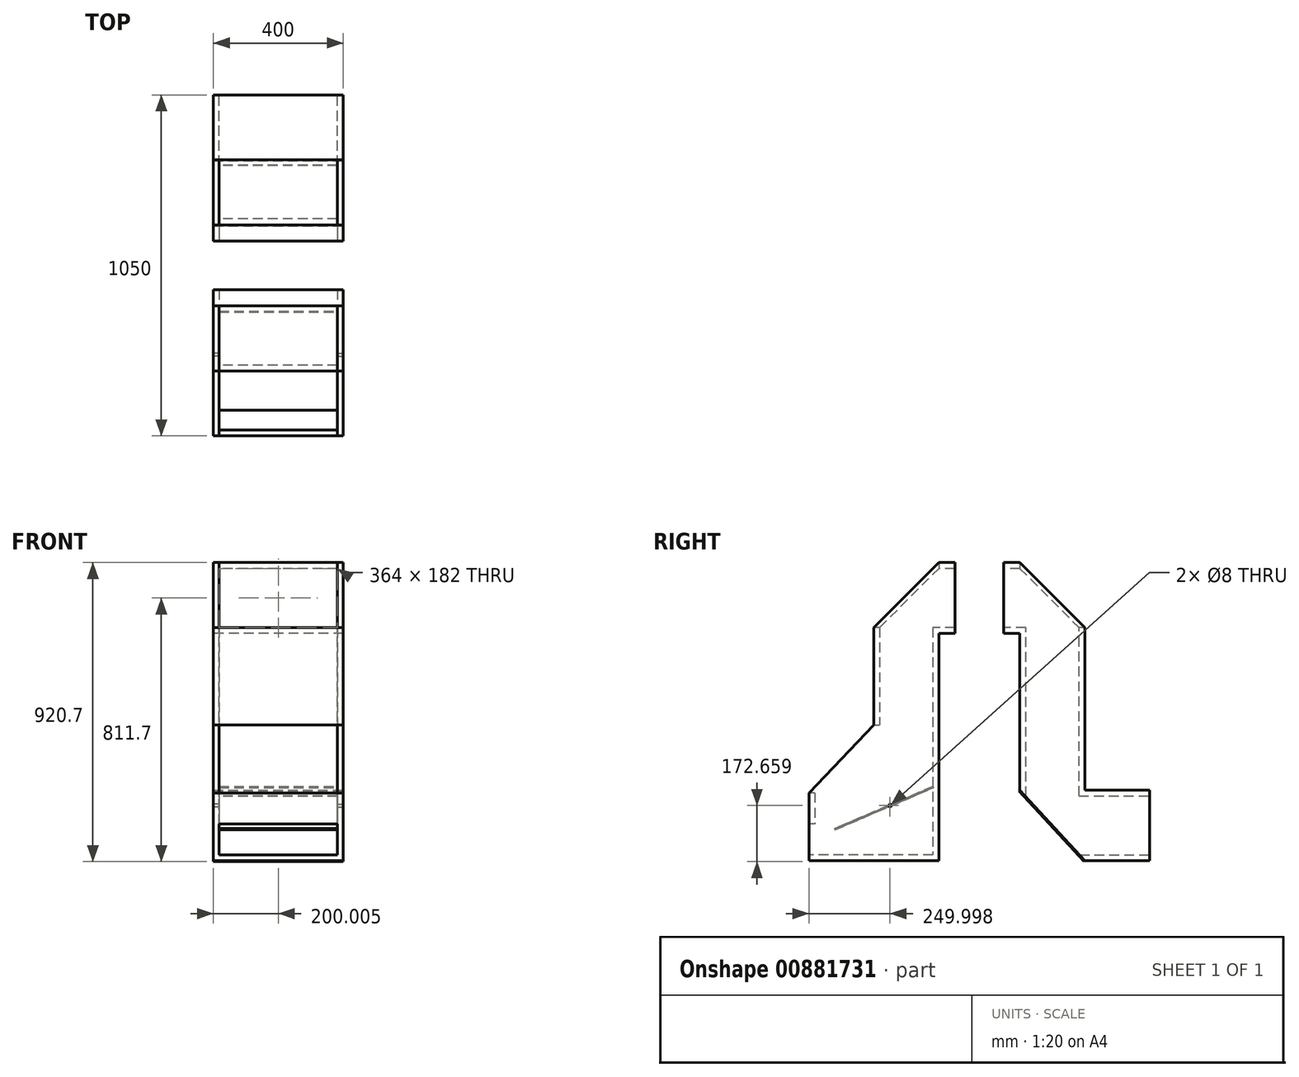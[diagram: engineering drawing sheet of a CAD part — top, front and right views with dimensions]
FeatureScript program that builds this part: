
annotation { "Feature Type Name" : "Feature", "Feature Type Description" : "" }
export const myFeature = defineFeature(function(context is Context, id is Id, definition is map)
    precondition{}
    {
        {
            var Q0;
            Q0=qCreatedBy(makeId("Top.planeOp"),FACE);
            var sketch = newSketch(context, id + "F0", { "sketchPlane" : qUnion([Q0])});
            skLineSegment(sketch, "E0.bottom", {"start": v(-193.3, 234.15) * mm, "end": v(206.7, 234.15) * mm});
            skLineSegment(sketch, "E0.top", {"start": v(-193.3, -165.85) * mm, "end": v(206.7, -165.85) * mm});
            skLineSegment(sketch, "E0.left", {"start": v(-193.3, 234.15) * mm, "end": v(-193.3, -165.85) * mm});
            skLineSegment(sketch, "E0.right", {"start": v(206.7, 234.15) * mm, "end": v(206.7, -165.85) * mm});
            skSolve(sketch);
        }
        {
            var Q0;
            Q0 = qSketchRegion(id + "F0", true);
            extrude(context, id + "F1", {"entities" : qUnion([Q0]), "oppositeDirection" : true, "depth" : 18 * mm, "offsetDistance" : 25 * mm});
        }
        {
            var Q0;
            Q0=makeQuery(id+"F1.opExtrude","CAP_FACE",FACE,{"disambiguationData":[OSD([sQuery(id+"F0.wireOp",EDGE,"E0.bottom"),sQuery(id+"F0.wireOp",EDGE,"E0.top"),sQuery(id+"F0.wireOp",EDGE,"E0.left"),sQuery(id+"F0.wireOp",EDGE,"E0.right")])],"isStart":true});
            var sketch = newSketch(context, id + "F2", { "sketchPlane" : qUnion([Q0])});
            skLineSegment(sketch, "E1.bottom", {"start": v(206.7, 234.15) * mm, "end": v(188.7, 234.15) * mm});
            skLineSegment(sketch, "E1.top", {"start": v(206.7, -165.85) * mm, "end": v(188.7, -165.85) * mm});
            skLineSegment(sketch, "E1.left", {"start": v(206.7, 234.15) * mm, "end": v(206.7, -165.85) * mm});
            skLineSegment(sketch, "E1.right", {"start": v(188.7, 234.15) * mm, "end": v(188.7, -165.85) * mm});
            skLineSegment(sketch, "E2.bottom", {"start": v(-193.3, 234.15) * mm, "end": v(-175.3, 234.15) * mm});
            skLineSegment(sketch, "E2.top", {"start": v(-193.3, -165.85) * mm, "end": v(-175.3, -165.85) * mm});
            skLineSegment(sketch, "E2.left", {"start": v(-193.3, 234.15) * mm, "end": v(-193.3, -165.85) * mm});
            skLineSegment(sketch, "E2.right", {"start": v(-175.3, 234.15) * mm, "end": v(-175.3, -165.85) * mm});
            skLineSegment(sketch, "E3.bottom", {"start": v(-175.3, 234.15) * mm, "end": v(188.7, 234.15) * mm});
            skLineSegment(sketch, "E3.top", {"start": v(-175.3, 216.15) * mm, "end": v(188.7, 216.15) * mm});
            skLineSegment(sketch, "E3.left", {"start": v(-175.3, 234.15) * mm, "end": v(-175.3, 216.15) * mm});
            skLineSegment(sketch, "E3.right", {"start": v(188.7, 234.15) * mm, "end": v(188.7, 216.15) * mm});
            skLineSegment(sketch, "E4.bottom", {"start": v(-175.3, -165.85) * mm, "end": v(188.7, -165.85) * mm});
            skLineSegment(sketch, "E4.top", {"start": v(-175.3, -147.85) * mm, "end": v(188.7, -147.85) * mm});
            skLineSegment(sketch, "E4.left", {"start": v(-175.3, -165.85) * mm, "end": v(-175.3, -147.85) * mm});
            skLineSegment(sketch, "E4.right", {"start": v(188.7, -165.85) * mm, "end": v(188.7, -147.85) * mm});
            skSolve(sketch);
        }
        {
            var Q0;
            Q0=makeQuery(id+"F2.imprint","IMPRINT",FACE,{"disambiguationData":[TD([[makeQuery(id+"F2.imprint","IMPRINT",EDGE,{"derivedFrom":sQuery(id+"F2.wireOp",EDGE,"E2.bottom")}),-1.0]])]});
            var Q1;
            Q1=makeQuery(id+"F2.imprint","IMPRINT",FACE,{"disambiguationData":[TD([[makeQuery(id+"F2.imprint","IMPRINT",EDGE,{"derivedFrom":sQuery(id+"F2.wireOp",EDGE,"E1.bottom")}),-1.0]])]});
            extrude(context, id + "F3", {"entities" : qUnion([Q0, Q1]), "operationType" : NewBodyOperationType.ADD, "depth" : 400 * mm, "offsetDistance" : 25 * mm});
        }
        {
            var Q0;
            Q0=makeQuery(id+"F2.imprint","IMPRINT",FACE,{"disambiguationData":[TD([[makeQuery(id+"F2.imprint","IMPRINT",EDGE,{"derivedFrom":sQuery(id+"F2.wireOp",EDGE,"E3.bottom")}),-1.0]])]});
            extrude(context, id + "F4", {"entities" : qUnion([Q0]), "operationType" : NewBodyOperationType.ADD, "depth" : 700 * mm, "offsetDistance" : 25 * mm});
        }
        {
            var Q0;
            Q0=makeQuery(id+"F3.boolean.opBoolean","MERGE",FACE,{"derivedFrom":[makeQuery(id+"F1.opExtrude","SWEPT_FACE",FACE,{"disambiguationData":[OSD([sQuery(id+"F0.wireOp",EDGE,"E0.right")])]}),makeQuery(id+"F3.opExtrude","SWEPT_FACE",FACE,{"disambiguationData":[OSD([sQuery(id+"F2.wireOp",EDGE,"E1.left")])]})]});
            var sketch = newSketch(context, id + "F5", { "sketchPlane" : qUnion([Q0])});
            skLineSegment(sketch, "E5", {"start": v(-165.85, 191) * mm, "end": v(34.15, 400) * mm});
            skSolve(sketch);
        }
        {
            var Q0;
            Q0=makeQuery(id+"F2.imprint","IMPRINT",FACE,{"disambiguationData":[TD([[makeQuery(id+"F2.imprint","IMPRINT",EDGE,{"derivedFrom":sQuery(id+"F2.wireOp",EDGE,"E4.bottom")}),1.0]])]});
            extrude(context, id + "F6", {"entities" : qUnion([Q0]), "operationType" : NewBodyOperationType.ADD, "depth" : (200 - 9) * mm, "offsetDistance" : 25 * mm});
        }
        {
            var Q0;
            Q0=makeQuery(id+"F6.boolean.opBoolean","MERGE",FACE,{"derivedFrom":[makeQuery(id+"F3.boolean.opBoolean","MERGE",FACE,{"derivedFrom":[makeQuery(id+"F1.opExtrude","SWEPT_FACE",FACE,{"disambiguationData":[OSD([sQuery(id+"F0.wireOp",EDGE,"E0.top")])]}),makeQuery(id+"F3.opExtrude","SWEPT_FACE",FACE,{"disambiguationData":[OSD([sQuery(id+"F2.wireOp",EDGE,"E1.top")])]}),makeQuery(id+"F3.opExtrude","SWEPT_FACE",FACE,{"disambiguationData":[OSD([sQuery(id+"F2.wireOp",EDGE,"E2.top")])]})]}),makeQuery(id+"F6.opExtrude","SWEPT_FACE",FACE,{"disambiguationData":[OSD([sQuery(id+"F2.wireOp",EDGE,"E4.bottom")])]})]});
            var sketch = newSketch(context, id + "F7", { "sketchPlane" : qUnion([Q0])});
            skLineSegment(sketch, "E6.bottom", {"start": v(-175.3, 0) * mm, "end": v(188.7, 0) * mm});
            skLineSegment(sketch, "E6.top", {"start": v(-175.3, 95.5) * mm, "end": v(188.7, 95.5) * mm});
            skLineSegment(sketch, "E6.left", {"start": v(-175.3, 0) * mm, "end": v(-175.3, 95.5) * mm});
            skLineSegment(sketch, "E6.right", {"start": v(188.7, 0) * mm, "end": v(188.7, 95.5) * mm});
            skSolve(sketch);
        }
        {
            var Q0;
            Q0 = qSketchRegion(id + "F7", true);
            extrude(context, id + "F8", {"entities" : qUnion([Q0]), "operationType" : NewBodyOperationType.REMOVE, "oppositeDirection" : true, "depth" : 25 * mm, "offsetDistance" : 25 * mm});
        }
        {
            var Q0;
            {var subQ0=sQuery(id+"F5.wireOp",EDGE,"E5");Q0=makeQuery(id+"F5.imprint","IMPRINT",FACE,{"disambiguationData":[TD([[makeQuery(id+"F5.imprint","IMPRINT",EDGE,{"derivedFrom":subQ0}),1.0]])]});}
            extrude(context, id + "F9", {"entities" : qUnion([Q0]), "operationType" : NewBodyOperationType.REMOVE, "endBound" : BoundingType.THROUGH_ALL, "oppositeDirection" : true, "depth" : 25 * mm, "offsetDistance" : 25 * mm});
        }
        {
            var Q0;
            Q0=makeQuery(id+"F3.opExtrude","CAP_FACE",FACE,{"disambiguationData":[OSD([sQuery(id+"F2.wireOp",EDGE,"E2.bottom"),sQuery(id+"F2.wireOp",EDGE,"E2.top"),sQuery(id+"F2.wireOp",EDGE,"E2.left"),sQuery(id+"F2.wireOp",EDGE,"E2.right"),sQuery(id+"F2.wireOp",EDGE,"E3.left"),sQuery(id+"F2.wireOp",EDGE,"E4.left")])],"isStart":false});
            extrude(context, id + "F10", {"entities" : qUnion([Q0]), "operationType" : NewBodyOperationType.ADD, "depth" : 300 * mm, "offsetDistance" : 25 * mm});
        }
        {
            var Q0;
            Q0=makeQuery(id+"F3.opExtrude","CAP_FACE",FACE,{"disambiguationData":[OSD([sQuery(id+"F2.wireOp",EDGE,"E1.bottom"),sQuery(id+"F2.wireOp",EDGE,"E1.top"),sQuery(id+"F2.wireOp",EDGE,"E1.left"),sQuery(id+"F2.wireOp",EDGE,"E1.right"),sQuery(id+"F2.wireOp",EDGE,"E3.right"),sQuery(id+"F2.wireOp",EDGE,"E4.right")])],"isStart":false});
            extrude(context, id + "F11", {"entities" : qUnion([Q0]), "operationType" : NewBodyOperationType.ADD, "depth" : 300 * mm, "offsetDistance" : 25 * mm});
        }
        {
            var Q0;
            {var subQ0=sQuery(id+"F2.wireOp",EDGE,"E4.left");var subQ1=sQuery(id+"F2.wireOp",EDGE,"E3.left");var subQ2=sQuery(id+"F2.wireOp",EDGE,"E2.right");Q0=makeQuery(id+"F10.boolean.opBoolean","MERGE",FACE,{"derivedFrom":[makeQuery(id+"F8.boolean.opBoolean","MERGE",FACE,{"derivedFrom":[makeQuery(id+"F3.opExtrude","SWEPT_FACE",FACE,{"disambiguationData":[OSD([subQ2,subQ1,subQ0])]})],"fromTools":[makeQuery(id+"F8.opExtrude","SWEPT_FACE",FACE,{"disambiguationData":[OSD([sQuery(id+"F7.wireOp",EDGE,"E6.left")])]})]}),makeQuery(id+"F10.opExtrude","SWEPT_FACE",FACE,{"disambiguationData":[OSD([subQ2,subQ1,subQ0])]})]});}
            var sketch = newSketch(context, id + "F12", { "sketchPlane" : qUnion([Q0])});
            skLineSegment(sketch, "E7.bottom", {"start": v(34.15, 700) * mm, "end": v(52.15, 700) * mm});
            skLineSegment(sketch, "E7.top", {"start": v(34.15, 400) * mm, "end": v(52.15, 400) * mm});
            skLineSegment(sketch, "E7.left", {"start": v(34.15, 700) * mm, "end": v(34.15, 400) * mm});
            skLineSegment(sketch, "E7.right", {"start": v(52.15, 700) * mm, "end": v(52.15, 400) * mm});
            skSolve(sketch);
        }
        {
            var Q0;
            Q0=makeQuery(id+"F12.imprint","IMPRINT",FACE,{"disambiguationData":[TD([[makeQuery(id+"F12.imprint","IMPRINT",EDGE,{"derivedFrom":sQuery(id+"F12.wireOp",EDGE,"E7.bottom")}),1.0]])]});
            var Q1;
            {var subQ0=sQuery(id+"F2.wireOp",EDGE,"E4.right");var subQ1=sQuery(id+"F2.wireOp",EDGE,"E3.right");var subQ2=sQuery(id+"F2.wireOp",EDGE,"E1.right");Q1=makeQuery(id+"F11.boolean.opBoolean","MERGE",FACE,{"derivedFrom":[makeQuery(id+"F8.boolean.opBoolean","MERGE",FACE,{"derivedFrom":[makeQuery(id+"F3.opExtrude","SWEPT_FACE",FACE,{"disambiguationData":[OSD([subQ2,subQ1,subQ0])]})],"fromTools":[makeQuery(id+"F8.opExtrude","SWEPT_FACE",FACE,{"disambiguationData":[OSD([sQuery(id+"F7.wireOp",EDGE,"E6.right")])]})]}),makeQuery(id+"F11.opExtrude","SWEPT_FACE",FACE,{"disambiguationData":[OSD([subQ2,subQ1,subQ0])]})]});}
            extrude(context, id + "F13", {"entities" : qUnion([Q0]), "operationType" : NewBodyOperationType.ADD, "endBound" : BoundingType.UP_TO_SURFACE, "depth" : 25 * mm, "endBoundEntityFace" : qUnion([Q1]), "offsetDistance" : 25 * mm});
        }
        {
            var Q0;
            {var subQ0=sQuery(id+"F2.wireOp",EDGE,"E1.left");Q0=makeQuery(id+"F11.boolean.opBoolean","MERGE",FACE,{"derivedFrom":[makeQuery(id+"F3.boolean.opBoolean","MERGE",FACE,{"derivedFrom":[makeQuery(id+"F1.opExtrude","SWEPT_FACE",FACE,{"disambiguationData":[OSD([sQuery(id+"F0.wireOp",EDGE,"E0.right")])]}),makeQuery(id+"F3.opExtrude","SWEPT_FACE",FACE,{"disambiguationData":[OSD([subQ0])]})]}),makeQuery(id+"F11.opExtrude","SWEPT_FACE",FACE,{"disambiguationData":[OSD([subQ0])]})]});}
            var sketch = newSketch(context, id + "F14", { "sketchPlane" : qUnion([Q0])});
            skLineSegment(sketch, "E8", {"start": v(-65.85, 295.5) * mm, "end": v(234.15, 8.42) * mm});
            skPoint(sketch, "E9", {"position": v(84.15, 151.96) * mm});
            skCircle(sketch, "E10", {"center": v(84.15, 151.96) * mm, "radius": 150 * mm});
            skCircle(sketch, "E11", {"center": v(84.15, 151.96) * mm, "radius": 4 * mm});
            skLineSegment(sketch, "E12", {"start": v(84.15, 151.96) * mm, "end": v(234.15, 151.96) * mm});
            skLineSegment(sketch, "E13", {"start": v(84.15, 151.96) * mm, "end": v(84.15, 301.96) * mm});
            skLineSegment(sketch, "E14", {"start": v(84.15, 151.96) * mm, "end": v(187.86, 260.33) * mm});
            skPoint(sketch, "E15", {"position": v(211, 206.15) * mm});
            skLineSegment(sketch, "E16", {"start": v(84.15, 151.96) * mm, "end": v(222.1, 210.88) * mm});
            skLineSegment(sketch, "E17", {"start": v(84.15, 151.96) * mm, "end": v(-53.8, 93.04) * mm});
            skSolve(sketch);
        }
        {
            var Q0;
            {var subQ0=sQuery(id+"F2.wireOp",EDGE,"E4.right");var subQ1=sQuery(id+"F2.wireOp",EDGE,"E3.right");var subQ2=sQuery(id+"F2.wireOp",EDGE,"E1.right");Q0=makeQuery(id+"F11.boolean.opBoolean","MERGE",FACE,{"derivedFrom":[makeQuery(id+"F8.boolean.opBoolean","MERGE",FACE,{"derivedFrom":[makeQuery(id+"F3.opExtrude","SWEPT_FACE",FACE,{"disambiguationData":[OSD([subQ2,subQ1,subQ0])]})],"fromTools":[makeQuery(id+"F8.opExtrude","SWEPT_FACE",FACE,{"disambiguationData":[OSD([sQuery(id+"F7.wireOp",EDGE,"E6.right")])]})]}),makeQuery(id+"F11.opExtrude","SWEPT_FACE",FACE,{"disambiguationData":[OSD([subQ2,subQ1,subQ0])]})]});}
            var sketch = newSketch(context, id + "F15", { "sketchPlane" : qUnion([Q0])});
            skLineSegment(sketch, "E18", {"start": v(-216.42, 210.63) * mm, "end": v(87.06, 81) * mm});
            skLineSegment(sketch, "E19", {"start": v(85.48, 77.32) * mm, "end": v(-217.99, 206.96) * mm});
            skPoint(sketch, "E20", {"position": v(-84.15, 151.96) * mm});
            skLineSegment(sketch, "E21", {"start": v(85.48, 77.32) * mm, "end": v(87.06, 81) * mm});
            skLineSegment(sketch, "E22", {"start": v(-216.42, 210.63) * mm, "end": v(-217.99, 206.96) * mm});
            skSolve(sketch);
        }
        {
            var Q0;
            Q0 = qSketchRegion(id + "F15", true);
            var Q1;
            {var subQ0=sQuery(id+"F2.wireOp",EDGE,"E4.left");var subQ1=sQuery(id+"F2.wireOp",EDGE,"E3.left");var subQ2=sQuery(id+"F2.wireOp",EDGE,"E2.right");Q1=makeQuery(id+"F10.boolean.opBoolean","MERGE",FACE,{"derivedFrom":[makeQuery(id+"F8.boolean.opBoolean","MERGE",FACE,{"derivedFrom":[makeQuery(id+"F3.opExtrude","SWEPT_FACE",FACE,{"disambiguationData":[OSD([subQ2,subQ1,subQ0])]})],"fromTools":[makeQuery(id+"F8.opExtrude","SWEPT_FACE",FACE,{"disambiguationData":[OSD([sQuery(id+"F7.wireOp",EDGE,"E6.left")])]})]}),makeQuery(id+"F10.opExtrude","SWEPT_FACE",FACE,{"disambiguationData":[OSD([subQ2,subQ1,subQ0])]})]});}
            extrude(context, id + "F16", {"entities" : qUnion([Q0]), "endBound" : BoundingType.UP_TO_SURFACE, "depth" : 25 * mm, "endBoundEntityFace" : qUnion([Q1]), "offsetDistance" : 25 * mm});
        }
        {
            var Q0;
            {var subQ1=sQuery(id+"F14.wireOp",EDGE,"E8");var subQ3=sQuery(id+"F14.wireOp",EDGE,"E11");var subQ4=makeQuery(id+"F14.imprint","INTERSECT",VERTEX,{"disambiguationData":[OD(1.0)],"derivedFrom":[subQ1,subQ3]});Q0=makeQuery(id+"F14.imprint","IMPRINT",FACE,{"disambiguationData":[TD([[makeQuery(id+"F14.imprint","IMPRINT",EDGE,{"disambiguationData":[TD([[subQ4,1.0]])],"derivedFrom":subQ3}),1.0]])]});}
            var Q1;
            {var subQ1=sQuery(id+"F14.wireOp",EDGE,"E8");var subQ3=sQuery(id+"F14.wireOp",EDGE,"E11");var subQ4=makeQuery(id+"F14.imprint","INTERSECT",VERTEX,{"disambiguationData":[OD(0.0)],"derivedFrom":[subQ1,subQ3]});Q1=makeQuery(id+"F14.imprint","IMPRINT",FACE,{"disambiguationData":[TD([[makeQuery(id+"F14.imprint","IMPRINT",EDGE,{"disambiguationData":[TD([[subQ4,-1.0]])],"derivedFrom":subQ3}),1.0]])]});}
            var Q2;
            {var subQ1=sQuery(id+"F14.wireOp",EDGE,"E8");var subQ3=sQuery(id+"F14.wireOp",EDGE,"E11");var subQ4=makeQuery(id+"F14.imprint","INTERSECT",VERTEX,{"disambiguationData":[OD(0.0)],"derivedFrom":[subQ1,subQ3]});Q2=makeQuery(id+"F14.imprint","IMPRINT",FACE,{"disambiguationData":[TD([[makeQuery(id+"F14.imprint","IMPRINT",EDGE,{"disambiguationData":[TD([[subQ4,1.0]])],"derivedFrom":subQ3}),1.0]])]});}
            var Q3;
            {var subQ0=sQuery(id+"F14.wireOp",EDGE,"E14");var subQ1=sQuery(id+"F14.wireOp",EDGE,"E11");var subQ2=makeQuery(id+"F14.imprint","INTERSECT",VERTEX,{"derivedFrom":[subQ1,subQ0]});Q3=makeQuery(id+"F14.imprint","IMPRINT",FACE,{"disambiguationData":[TD([[makeQuery(id+"F14.imprint","IMPRINT",EDGE,{"disambiguationData":[TD([[subQ2,-1.0]])],"derivedFrom":subQ1}),1.0]])]});}
            var Q4;
            {var subQ0=sQuery(id+"F14.wireOp",EDGE,"E16");var subQ1=sQuery(id+"F14.wireOp",EDGE,"E11");var subQ2=makeQuery(id+"F14.imprint","INTERSECT",VERTEX,{"derivedFrom":[subQ1,subQ0]});Q4=makeQuery(id+"F14.imprint","IMPRINT",FACE,{"disambiguationData":[TD([[makeQuery(id+"F14.imprint","IMPRINT",EDGE,{"disambiguationData":[TD([[subQ2,-1.0]])],"derivedFrom":subQ1}),1.0]])]});}
            var Q5;
            {var subQ0=sQuery(id+"F14.wireOp",EDGE,"E16");var subQ1=sQuery(id+"F14.wireOp",EDGE,"E11");var subQ2=makeQuery(id+"F14.imprint","INTERSECT",VERTEX,{"derivedFrom":[subQ1,subQ0]});Q5=makeQuery(id+"F14.imprint","IMPRINT",FACE,{"disambiguationData":[TD([[makeQuery(id+"F14.imprint","IMPRINT",EDGE,{"disambiguationData":[TD([[subQ2,1.0]])],"derivedFrom":subQ1}),1.0]])]});}
            var Q6;
            {var subQ1=sQuery(id+"F14.wireOp",EDGE,"E8");var subQ3=sQuery(id+"F14.wireOp",EDGE,"E11");var subQ4=makeQuery(id+"F14.imprint","INTERSECT",VERTEX,{"disambiguationData":[OD(1.0)],"derivedFrom":[subQ1,subQ3]});Q6=makeQuery(id+"F14.imprint","IMPRINT",FACE,{"disambiguationData":[TD([[makeQuery(id+"F14.imprint","IMPRINT",EDGE,{"disambiguationData":[TD([[subQ4,-1.0]])],"derivedFrom":subQ3}),1.0]])]});}
            extrude(context, id + "F17", {"entities" : qUnion([Q0, Q1, Q2, Q3, Q4, Q5, Q6]), "operationType" : NewBodyOperationType.REMOVE, "oppositeDirection" : true, "depth" : 18 * mm, "offsetDistance" : 25 * mm});
        }
        {
            var Q0;
            {var subQ0=sQuery(id+"F2.wireOp",EDGE,"E2.left");Q0=makeQuery(id+"F10.boolean.opBoolean","MERGE",FACE,{"derivedFrom":[makeQuery(id+"F3.boolean.opBoolean","MERGE",FACE,{"derivedFrom":[makeQuery(id+"F1.opExtrude","SWEPT_FACE",FACE,{"disambiguationData":[OSD([sQuery(id+"F0.wireOp",EDGE,"E0.left")])]}),makeQuery(id+"F3.opExtrude","SWEPT_FACE",FACE,{"disambiguationData":[OSD([subQ0])]})]}),makeQuery(id+"F10.opExtrude","SWEPT_FACE",FACE,{"disambiguationData":[OSD([subQ0])]})]});}
            var sketch = newSketch(context, id + "F18", { "sketchPlane" : qUnion([Q0])});
            skPoint(sketch, "E23", {"position": v(-84.15, 151.96) * mm});
            skCircle(sketch, "E24", {"center": v(-84.15, 151.96) * mm, "radius": 4 * mm});
            skSolve(sketch);
        }
        {
            var Q0;
            Q0 = qSketchRegion(id + "F18", true);
            extrude(context, id + "F19", {"entities" : qUnion([Q0]), "operationType" : NewBodyOperationType.REMOVE, "oppositeDirection" : true, "depth" : 18 * mm, "offsetDistance" : 25 * mm});
        }
        {
            var Q0;
            {var subQ0=sQuery(id+"F2.wireOp",EDGE,"E3.right");var subQ1=sQuery(id+"F2.wireOp",EDGE,"E3.left");Q0=makeQuery(id+"F13.boolean.opBoolean","MERGE",FACE,{"derivedFrom":[makeQuery(id+"F11.boolean.opBoolean","MERGE",FACE,{"derivedFrom":[makeQuery(id+"F10.boolean.opBoolean","MERGE",FACE,{"derivedFrom":[makeQuery(id+"F4.opExtrude","CAP_FACE",FACE,{"disambiguationData":[OSD([sQuery(id+"F2.wireOp",EDGE,"E3.bottom"),sQuery(id+"F2.wireOp",EDGE,"E3.top"),subQ1,subQ0])],"isStart":false}),makeQuery(id+"F10.opExtrude","CAP_FACE",FACE,{"disambiguationData":[OSD([sQuery(id+"F2.wireOp",EDGE,"E2.bottom"),sQuery(id+"F2.wireOp",EDGE,"E2.top"),sQuery(id+"F2.wireOp",EDGE,"E2.left"),sQuery(id+"F2.wireOp",EDGE,"E2.right"),subQ1,sQuery(id+"F2.wireOp",EDGE,"E4.left")])],"isStart":false})]}),makeQuery(id+"F11.opExtrude","CAP_FACE",FACE,{"disambiguationData":[OSD([sQuery(id+"F2.wireOp",EDGE,"E1.bottom"),sQuery(id+"F2.wireOp",EDGE,"E1.top"),sQuery(id+"F2.wireOp",EDGE,"E1.left"),sQuery(id+"F2.wireOp",EDGE,"E1.right"),subQ0,sQuery(id+"F2.wireOp",EDGE,"E4.right")])],"isStart":false})]}),makeQuery(id+"F13.opExtrude","SWEPT_FACE",FACE,{"disambiguationData":[OSD([sQuery(id+"F12.wireOp",EDGE,"E7.bottom")])]})]});}
            var sketch = newSketch(context, id + "F20", { "sketchPlane" : qUnion([Q0])});
            skLineSegment(sketch, "E25.bottom", {"start": v(-193.3, 234.15) * mm, "end": v(-175.3, 234.15) * mm});
            skLineSegment(sketch, "E25.top", {"start": v(-193.3, 34.15) * mm, "end": v(-175.3, 34.15) * mm});
            skLineSegment(sketch, "E25.left", {"start": v(-193.3, 234.15) * mm, "end": v(-193.3, 34.15) * mm});
            skLineSegment(sketch, "E25.right", {"start": v(-175.3, 234.15) * mm, "end": v(-175.3, 34.15) * mm});
            skLineSegment(sketch, "E26.bottom", {"start": v(206.7, 234.15) * mm, "end": v(188.7, 234.15) * mm});
            skLineSegment(sketch, "E26.top", {"start": v(206.7, 34.15) * mm, "end": v(188.7, 34.15) * mm});
            skLineSegment(sketch, "E26.left", {"start": v(206.7, 234.15) * mm, "end": v(206.7, 34.15) * mm});
            skLineSegment(sketch, "E26.right", {"start": v(188.7, 234.15) * mm, "end": v(188.7, 34.15) * mm});
            skSolve(sketch);
        }
        {
            var Q0;
            Q0 = qSketchRegion(id + "F20", true);
            extrude(context, id + "F21", {"entities" : qUnion([Q0]), "operationType" : NewBodyOperationType.ADD, "depth" : 200 * mm, "offsetDistance" : 25 * mm});
        }
        {
            var Q0;
            {var subQ0=sQuery(id+"F2.wireOp",EDGE,"E1.left");Q0=makeQuery(id+"F21.boolean.opBoolean","MERGE",FACE,{"derivedFrom":[makeQuery(id+"F11.boolean.opBoolean","MERGE",FACE,{"derivedFrom":[makeQuery(id+"F3.boolean.opBoolean","MERGE",FACE,{"derivedFrom":[makeQuery(id+"F1.opExtrude","SWEPT_FACE",FACE,{"disambiguationData":[OSD([sQuery(id+"F0.wireOp",EDGE,"E0.right")])]}),makeQuery(id+"F3.opExtrude","SWEPT_FACE",FACE,{"disambiguationData":[OSD([subQ0])]})]}),makeQuery(id+"F11.opExtrude","SWEPT_FACE",FACE,{"disambiguationData":[OSD([subQ0])]})]}),makeQuery(id+"F21.opExtrude","SWEPT_FACE",FACE,{"disambiguationData":[OSD([sQuery(id+"F20.wireOp",EDGE,"E26.left")])]})]});}
            var sketch = newSketch(context, id + "F22", { "sketchPlane" : qUnion([Q0])});
            skPoint(sketch, "E27", {"position": v(34.15, 700) * mm});
            skLineSegment(sketch, "E28", {"start": v(34.15, 700) * mm, "end": v(234.15, 900) * mm});
            skSolve(sketch);
        }
        {
            var Q0;
            {var subQ0=sQuery(id+"F22.wireOp",EDGE,"E28");Q0=makeQuery(id+"F22.imprint","IMPRINT",FACE,{"disambiguationData":[TD([[makeQuery(id+"F22.imprint","IMPRINT",EDGE,{"derivedFrom":subQ0}),1.0]])]});}
            extrude(context, id + "F23", {"entities" : qUnion([Q0]), "operationType" : NewBodyOperationType.REMOVE, "endBound" : BoundingType.THROUGH_ALL, "oppositeDirection" : true, "depth" : 25 * mm, "offsetDistance" : 25 * mm});
        }
        {
            var Q0;
            {var subQ0=sQuery(id+"F2.wireOp",EDGE,"E1.bottom");var subQ1=sQuery(id+"F2.wireOp",EDGE,"E2.bottom");Q0=makeQuery(id+"F21.boolean.opBoolean","MERGE",FACE,{"derivedFrom":[makeQuery(id+"F11.boolean.opBoolean","MERGE",FACE,{"derivedFrom":[makeQuery(id+"F10.boolean.opBoolean","MERGE",FACE,{"derivedFrom":[makeQuery(id+"F4.boolean.opBoolean","MERGE",FACE,{"derivedFrom":[makeQuery(id+"F3.boolean.opBoolean","MERGE",FACE,{"derivedFrom":[makeQuery(id+"F1.opExtrude","SWEPT_FACE",FACE,{"disambiguationData":[OSD([sQuery(id+"F0.wireOp",EDGE,"E0.bottom")])]}),makeQuery(id+"F3.opExtrude","SWEPT_FACE",FACE,{"disambiguationData":[OSD([subQ0])]}),makeQuery(id+"F3.opExtrude","SWEPT_FACE",FACE,{"disambiguationData":[OSD([subQ1])]})]}),makeQuery(id+"F4.opExtrude","SWEPT_FACE",FACE,{"disambiguationData":[OSD([sQuery(id+"F2.wireOp",EDGE,"E3.bottom")])]})]}),makeQuery(id+"F10.opExtrude","SWEPT_FACE",FACE,{"disambiguationData":[OSD([subQ1])]})]}),makeQuery(id+"F11.opExtrude","SWEPT_FACE",FACE,{"disambiguationData":[OSD([subQ0])]})]}),makeQuery(id+"F21.opExtrude","SWEPT_FACE",FACE,{"disambiguationData":[OSD([sQuery(id+"F20.wireOp",EDGE,"E25.bottom")])]}),makeQuery(id+"F21.opExtrude","SWEPT_FACE",FACE,{"disambiguationData":[OSD([sQuery(id+"F20.wireOp",EDGE,"E26.bottom")])]})]});}
            var sketch = newSketch(context, id + "F24", { "sketchPlane" : qUnion([Q0])});
            skLineSegment(sketch, "E29.bottom", {"start": v(-206.7, 900) * mm, "end": v(-188.7, 900) * mm});
            skLineSegment(sketch, "E29.top", {"start": v(-206.7, 700) * mm, "end": v(-188.7, 700) * mm});
            skLineSegment(sketch, "E29.left", {"start": v(-206.7, 900) * mm, "end": v(-206.7, 700) * mm});
            skLineSegment(sketch, "E29.right", {"start": v(-188.7, 900) * mm, "end": v(-188.7, 700) * mm});
            skLineSegment(sketch, "E30.bottom", {"start": v(175.3, 900) * mm, "end": v(193.3, 900) * mm});
            skLineSegment(sketch, "E30.top", {"start": v(175.3, 700) * mm, "end": v(193.3, 700) * mm});
            skLineSegment(sketch, "E30.left", {"start": v(175.3, 900) * mm, "end": v(175.3, 700) * mm});
            skLineSegment(sketch, "E30.right", {"start": v(193.3, 900) * mm, "end": v(193.3, 700) * mm});
            skLineSegment(sketch, "E31.bottom", {"start": v(-206.7, 700) * mm, "end": v(193.3, 700) * mm});
            skLineSegment(sketch, "E31.top", {"start": v(-206.7, 682) * mm, "end": v(193.3, 682) * mm});
            skLineSegment(sketch, "E31.left", {"start": v(-206.7, 700) * mm, "end": v(-206.7, 682) * mm});
            skLineSegment(sketch, "E31.right", {"start": v(193.3, 700) * mm, "end": v(193.3, 682) * mm});
            skLineSegment(sketch, "E32.bottom", {"start": v(-206.7, 900) * mm, "end": v(193.3, 900) * mm});
            skLineSegment(sketch, "E32.top", {"start": v(-206.7, 882) * mm, "end": v(193.3, 882) * mm});
            skLineSegment(sketch, "E32.left", {"start": v(-206.7, 900) * mm, "end": v(-206.7, 882) * mm});
            skLineSegment(sketch, "E32.right", {"start": v(193.3, 900) * mm, "end": v(193.3, 882) * mm});
            skSolve(sketch);
        }
        {
            var Q0;
            Q0 = qSketchRegion(id + "F24", true);
            extrude(context, id + "F25", {"entities" : qUnion([Q0]), "operationType" : NewBodyOperationType.ADD, "depth" : 50 * mm, "offsetDistance" : 25 * mm});
        }
        {
            var Q0;
            Q0=makeQuery(id+"F25.opExtrude","CAP_FACE",FACE,{"disambiguationData":[OSD([sQuery(id+"F24.wireOp",EDGE,"E29.left"),sQuery(id+"F24.wireOp",EDGE,"E29.right"),sQuery(id+"F24.wireOp",EDGE,"E30.left"),sQuery(id+"F24.wireOp",EDGE,"E30.right"),sQuery(id+"F24.wireOp",EDGE,"E31.bottom"),sQuery(id+"F24.wireOp",EDGE,"E31.top"),sQuery(id+"F24.wireOp",EDGE,"E31.left"),sQuery(id+"F24.wireOp",EDGE,"E31.right"),sQuery(id+"F24.wireOp",EDGE,"E32.bottom"),sQuery(id+"F24.wireOp",EDGE,"E32.top"),sQuery(id+"F24.wireOp",EDGE,"E32.left"),sQuery(id+"F24.wireOp",EDGE,"E32.right")])],"isStart":false});
            cPlane(context, id + "F26", {"entities" : qUnion([Q0]), "cplaneType" : CPlaneType.OFFSET, "offset" : 200 * mm, "width" : 150 * mm, "height" : 150 * mm});
        }
        {
            var Q0;
            Q0=qCreatedBy(id+"F26.planeOp",FACE);
            var sketch = newSketch(context, id + "F27", { "sketchPlane" : qUnion([Q0])});
            skPoint(sketch, "E33", {"position": v(-206.7, 900) * mm});
            skPoint(sketch, "E34", {"position": v(-206.7, 682) * mm});
            skPoint(sketch, "E35", {"position": v(193.3, 900) * mm});
            skPoint(sketch, "E36", {"position": v(193.3, 682) * mm});
            skPoint(sketch, "E37", {"position": v(-188.7, 700) * mm});
            skPoint(sketch, "E38", {"position": v(-188.7, 882) * mm});
            skPoint(sketch, "E39", {"position": v(175.3, 882) * mm});
            skPoint(sketch, "E40", {"position": v(175.3, 700) * mm});
            skLineSegment(sketch, "E41", {"start": v(-206.7, 900) * mm, "end": v(193.3, 900) * mm});
            skLineSegment(sketch, "E42", {"start": v(193.3, 682) * mm, "end": v(-206.7, 682) * mm});
            skLineSegment(sketch, "E43", {"start": v(-206.7, 900) * mm, "end": v(-206.7, 682) * mm});
            skLineSegment(sketch, "E44", {"start": v(193.3, 900) * mm, "end": v(193.3, 682) * mm});
            skLineSegment(sketch, "E45", {"start": v(175.3, 882) * mm, "end": v(175.3, 700) * mm});
            skLineSegment(sketch, "E46", {"start": v(-188.7, 700) * mm, "end": v(-188.7, 882) * mm});
            skLineSegment(sketch, "E47", {"start": v(-188.7, 882) * mm, "end": v(175.3, 882) * mm});
            skLineSegment(sketch, "E48", {"start": v(175.3, 700) * mm, "end": v(-188.7, 700) * mm});
            skSolve(sketch);
        }
        {
            var Q0;
            Q0=makeQuery(id+"F27.imprint","IMPRINT",FACE,{"disambiguationData":[TD([[makeQuery(id+"F27.imprint","IMPRINT",EDGE,{"derivedFrom":sQuery(id+"F27.wireOp",EDGE,"E41")}),-1.0]])]});
            extrude(context, id + "F28", {"entities" : qUnion([Q0]), "depth" : 200 * mm, "offsetDistance" : 25 * mm});
        }
        {
            var Q0;
            Q0=makeQuery(id+"F28.opExtrude","SWEPT_FACE",FACE,{"disambiguationData":[OSD([sQuery(id+"F27.wireOp",EDGE,"E42")])]});
            var sketch = newSketch(context, id + "F29", { "sketchPlane" : qUnion([Q0])});
            skPoint(sketch, "E49", {"position": v(188.7, -684.15) * mm});
            skLineSegment(sketch, "E50.bottom", {"start": v(206.7, -484.15) * mm, "end": v(188.7, -484.15) * mm});
            skLineSegment(sketch, "E50.top", {"start": v(206.7, -684.15) * mm, "end": v(188.7, -684.15) * mm});
            skLineSegment(sketch, "E50.left", {"start": v(206.7, -484.15) * mm, "end": v(206.7, -684.15) * mm});
            skLineSegment(sketch, "E50.right", {"start": v(188.7, -484.15) * mm, "end": v(188.7, -684.15) * mm});
            skPoint(sketch, "E51", {"position": v(-175.3, -684.15) * mm});
            skLineSegment(sketch, "E52.bottom", {"start": v(-193.3, -484.15) * mm, "end": v(-175.3, -484.15) * mm});
            skLineSegment(sketch, "E52.top", {"start": v(-193.3, -684.15) * mm, "end": v(-175.3, -684.15) * mm});
            skLineSegment(sketch, "E52.left", {"start": v(-193.3, -484.15) * mm, "end": v(-193.3, -684.15) * mm});
            skLineSegment(sketch, "E52.right", {"start": v(-175.3, -484.15) * mm, "end": v(-175.3, -684.15) * mm});
            skLineSegment(sketch, "E53.bottom", {"start": v(188.7, -484.15) * mm, "end": v(-175.3, -484.15) * mm});
            skLineSegment(sketch, "E53.top", {"start": v(188.7, -502.15) * mm, "end": v(-175.3, -502.15) * mm});
            skLineSegment(sketch, "E53.left", {"start": v(188.7, -484.15) * mm, "end": v(188.7, -502.15) * mm});
            skLineSegment(sketch, "E53.right", {"start": v(-175.3, -484.15) * mm, "end": v(-175.3, -502.15) * mm});
            skLineSegment(sketch, "E54.bottom", {"start": v(188.7, -684.15) * mm, "end": v(-175.3, -684.15) * mm});
            skLineSegment(sketch, "E54.top", {"start": v(188.7, -666.15) * mm, "end": v(-175.3, -666.15) * mm});
            skLineSegment(sketch, "E54.left", {"start": v(188.7, -684.15) * mm, "end": v(188.7, -666.15) * mm});
            skLineSegment(sketch, "E54.right", {"start": v(-175.3, -684.15) * mm, "end": v(-175.3, -666.15) * mm});
            skSolve(sketch);
        }
        {
            var Q0;
            Q0 = qSketchRegion(id + "F29", true);
            extrude(context, id + "F30", {"entities" : qUnion([Q0]), "operationType" : NewBodyOperationType.ADD, "depth" : 700 * mm, "offsetDistance" : 25 * mm});
        }
        {
            var Q0;
            Q0=makeQuery(id+"F28.opExtrude","SWEPT_FACE",FACE,{"disambiguationData":[OSD([sQuery(id+"F27.wireOp",EDGE,"E42")])]});
            extrude(context, id + "F31", {"entities" : qUnion([Q0]), "operationType" : NewBodyOperationType.REMOVE, "oppositeDirection" : true, "depth" : 25 * mm, "offsetDistance" : 25 * mm});
        }
        {
            var Q0;
            Q0=makeQuery(id+"F30.boolean.opBoolean","MERGE",FACE,{"derivedFrom":[makeQuery(id+"F28.opExtrude","SWEPT_FACE",FACE,{"disambiguationData":[OSD([sQuery(id+"F27.wireOp",EDGE,"E43")])]}),makeQuery(id+"F30.opExtrude","SWEPT_FACE",FACE,{"disambiguationData":[OSD([sQuery(id+"F29.wireOp",EDGE,"E50.left")])]})]});
            var sketch = newSketch(context, id + "F32", { "sketchPlane" : qUnion([Q0])});
            skPoint(sketch, "E55", {"position": v(684.15, 700) * mm});
            skLineSegment(sketch, "E56", {"start": v(684.15, 700) * mm, "end": v(484.15, 900) * mm});
            skSolve(sketch);
        }
        {
            var Q0;
            {var subQ0=sQuery(id+"F32.wireOp",EDGE,"E56");Q0=makeQuery(id+"F32.imprint","IMPRINT",FACE,{"disambiguationData":[TD([[makeQuery(id+"F32.imprint","IMPRINT",EDGE,{"derivedFrom":subQ0}),-1.0]])]});}
            extrude(context, id + "F33", {"entities" : qUnion([Q0]), "operationType" : NewBodyOperationType.REMOVE, "endBound" : BoundingType.THROUGH_ALL, "oppositeDirection" : true, "depth" : 25 * mm, "offsetDistance" : 25 * mm});
        }
        {
            var Q0;
            {var subQ0=sQuery(id+"F2.wireOp",EDGE,"E4.left");var subQ1=sQuery(id+"F2.wireOp",EDGE,"E3.left");var subQ2=sQuery(id+"F2.wireOp",EDGE,"E2.right");Q0=makeQuery(id+"F25.boolean.opBoolean","MERGE",FACE,{"derivedFrom":[makeQuery(id+"F21.boolean.opBoolean","MERGE",FACE,{"derivedFrom":[makeQuery(id+"F10.boolean.opBoolean","MERGE",FACE,{"derivedFrom":[makeQuery(id+"F8.boolean.opBoolean","MERGE",FACE,{"derivedFrom":[makeQuery(id+"F3.opExtrude","SWEPT_FACE",FACE,{"disambiguationData":[OSD([subQ2,subQ1,subQ0])]})],"fromTools":[makeQuery(id+"F8.opExtrude","SWEPT_FACE",FACE,{"disambiguationData":[OSD([sQuery(id+"F7.wireOp",EDGE,"E6.left")])]})]}),makeQuery(id+"F10.opExtrude","SWEPT_FACE",FACE,{"disambiguationData":[OSD([subQ2,subQ1,subQ0])]})]}),makeQuery(id+"F21.opExtrude","SWEPT_FACE",FACE,{"disambiguationData":[OSD([sQuery(id+"F20.wireOp",EDGE,"E25.right")])]})]}),makeQuery(id+"F25.opExtrude","SWEPT_FACE",FACE,{"disambiguationData":[OSD([sQuery(id+"F24.wireOp",EDGE,"E30.left")])]})]});}
            var sketch = newSketch(context, id + "F34", { "sketchPlane" : qUnion([Q0])});
            skLineSegment(sketch, "E57", {"start": v(34.15, 700) * mm, "end": v(52.15, 700) * mm});
            skLineSegment(sketch, "E58", {"start": v(52.15, 700) * mm, "end": v(234.15, 882) * mm});
            skLineSegment(sketch, "E59", {"start": v(234.15, 882) * mm, "end": v(234.15, 900) * mm});
            skLineSegment(sketch, "E60", {"start": v(234.15, 900) * mm, "end": v(34.15, 700) * mm});
            skSolve(sketch);
        }
        {
            var Q0;
            Q0 = qSketchRegion(id + "F34", true);
            var Q1;
            {var subQ0=sQuery(id+"F2.wireOp",EDGE,"E4.right");var subQ1=sQuery(id+"F2.wireOp",EDGE,"E3.right");var subQ2=sQuery(id+"F2.wireOp",EDGE,"E1.right");Q1=makeQuery(id+"F25.boolean.opBoolean","MERGE",FACE,{"derivedFrom":[makeQuery(id+"F21.boolean.opBoolean","MERGE",FACE,{"derivedFrom":[makeQuery(id+"F11.boolean.opBoolean","MERGE",FACE,{"derivedFrom":[makeQuery(id+"F8.boolean.opBoolean","MERGE",FACE,{"derivedFrom":[makeQuery(id+"F3.opExtrude","SWEPT_FACE",FACE,{"disambiguationData":[OSD([subQ2,subQ1,subQ0])]})],"fromTools":[makeQuery(id+"F8.opExtrude","SWEPT_FACE",FACE,{"disambiguationData":[OSD([sQuery(id+"F7.wireOp",EDGE,"E6.right")])]})]}),makeQuery(id+"F11.opExtrude","SWEPT_FACE",FACE,{"disambiguationData":[OSD([subQ2,subQ1,subQ0])]})]}),makeQuery(id+"F21.opExtrude","SWEPT_FACE",FACE,{"disambiguationData":[OSD([sQuery(id+"F20.wireOp",EDGE,"E26.right")])]})]}),makeQuery(id+"F25.opExtrude","SWEPT_FACE",FACE,{"disambiguationData":[OSD([sQuery(id+"F24.wireOp",EDGE,"E29.right")])]})]});}
            extrude(context, id + "F35", {"entities" : qUnion([Q0]), "endBound" : BoundingType.UP_TO_SURFACE, "depth" : 25 * mm, "endBoundEntityFace" : qUnion([Q1]), "offsetDistance" : 25 * mm});
        }
        {
            var Q0;
            Q0=makeQuery(id+"F30.boolean.opBoolean","MERGE",FACE,{"derivedFrom":[makeQuery(id+"F28.opExtrude","CAP_FACE",FACE,{"disambiguationData":[OSD([sQuery(id+"F27.wireOp",EDGE,"E41"),sQuery(id+"F27.wireOp",EDGE,"E42"),sQuery(id+"F27.wireOp",EDGE,"E43"),sQuery(id+"F27.wireOp",EDGE,"E44"),sQuery(id+"F27.wireOp",EDGE,"E45"),sQuery(id+"F27.wireOp",EDGE,"E46"),sQuery(id+"F27.wireOp",EDGE,"E47"),sQuery(id+"F27.wireOp",EDGE,"E48")])],"isStart":true}),makeQuery(id+"F30.opExtrude","SWEPT_FACE",FACE,{"disambiguationData":[OSD([sQuery(id+"F29.wireOp",EDGE,"E50.bottom"),sQuery(id+"F29.wireOp",EDGE,"E52.bottom"),sQuery(id+"F29.wireOp",EDGE,"E53.bottom")])]})]});
            var sketch = newSketch(context, id + "F36", { "sketchPlane" : qUnion([Q0])});
            skLineSegment(sketch, "E61.bottom", {"start": v(-193.3, 900) * mm, "end": v(206.7, 900) * mm});
            skLineSegment(sketch, "E61.top", {"start": v(-193.3, 882) * mm, "end": v(206.7, 882) * mm});
            skLineSegment(sketch, "E61.left", {"start": v(-193.3, 900) * mm, "end": v(-193.3, 882) * mm});
            skLineSegment(sketch, "E61.right", {"start": v(206.7, 900) * mm, "end": v(206.7, 882) * mm});
            skLineSegment(sketch, "E62.bottom", {"start": v(206.7, 700) * mm, "end": v(-193.3, 700) * mm});
            skLineSegment(sketch, "E62.top", {"start": v(206.7, 682) * mm, "end": v(-193.3, 682) * mm});
            skLineSegment(sketch, "E62.left", {"start": v(206.7, 700) * mm, "end": v(206.7, 682) * mm});
            skLineSegment(sketch, "E62.right", {"start": v(-193.3, 700) * mm, "end": v(-193.3, 682) * mm});
            skLineSegment(sketch, "E63.bottom", {"start": v(-193.3, 882) * mm, "end": v(-175.3, 882) * mm});
            skLineSegment(sketch, "E63.top", {"start": v(-193.3, 700) * mm, "end": v(-175.3, 700) * mm});
            skLineSegment(sketch, "E63.left", {"start": v(-193.3, 882) * mm, "end": v(-193.3, 700) * mm});
            skLineSegment(sketch, "E63.right", {"start": v(-175.3, 882) * mm, "end": v(-175.3, 700) * mm});
            skLineSegment(sketch, "E64.bottom", {"start": v(206.7, 882) * mm, "end": v(188.7, 882) * mm});
            skLineSegment(sketch, "E64.top", {"start": v(206.7, 700) * mm, "end": v(188.7, 700) * mm});
            skLineSegment(sketch, "E64.left", {"start": v(206.7, 882) * mm, "end": v(206.7, 700) * mm});
            skLineSegment(sketch, "E64.right", {"start": v(188.7, 882) * mm, "end": v(188.7, 700) * mm});
            skSolve(sketch);
        }
        {
            var Q0;
            Q0 = qSketchRegion(id + "F36", true);
            extrude(context, id + "F37", {"entities" : qUnion([Q0]), "operationType" : NewBodyOperationType.ADD, "depth" : 50 * mm, "offsetDistance" : 25 * mm});
        }
        {
            var Q0;
            Q0=makeQuery(id+"F37.boolean.opBoolean","MERGE",FACE,{"derivedFrom":[makeQuery(id+"F28.opExtrude","SWEPT_FACE",FACE,{"disambiguationData":[OSD([sQuery(id+"F27.wireOp",EDGE,"E47")])]}),makeQuery(id+"F37.opExtrude","SWEPT_FACE",FACE,{"disambiguationData":[OSD([sQuery(id+"F36.wireOp",EDGE,"E61.top")])]})]});
            var sketch = newSketch(context, id + "F38", { "sketchPlane" : qUnion([Q0])});
            skLineSegment(sketch, "E65.bottom", {"start": v(188.7, -502.15) * mm, "end": v(-175.3, -502.15) * mm});
            skLineSegment(sketch, "E65.top", {"start": v(188.7, -484.15) * mm, "end": v(-175.3, -484.15) * mm});
            skLineSegment(sketch, "E65.left", {"start": v(188.7, -502.15) * mm, "end": v(188.7, -484.15) * mm});
            skLineSegment(sketch, "E65.right", {"start": v(-175.3, -502.15) * mm, "end": v(-175.3, -484.15) * mm});
            skSolve(sketch);
        }
        {
            var Q0;
            Q0 = qSketchRegion(id + "F38", true);
            extrude(context, id + "F39", {"entities" : qUnion([Q0]), "operationType" : NewBodyOperationType.REMOVE, "oppositeDirection" : true, "depth" : 25 * mm, "offsetDistance" : 25 * mm});
        }
        {
            var Q0;
            {var subQ0=sQuery(id+"F29.wireOp",EDGE,"E52.right");Q0=makeQuery(id+"F39.boolean.opBoolean","MERGE",FACE,{"derivedFrom":[makeQuery(id+"F37.boolean.opBoolean","MERGE",FACE,{"derivedFrom":[makeQuery(id+"F31.boolean.opBoolean","MERGE",FACE,{"derivedFrom":[makeQuery(id+"F28.opExtrude","SWEPT_FACE",FACE,{"disambiguationData":[OSD([sQuery(id+"F27.wireOp",EDGE,"E45")])]}),makeQuery(id+"F30.opExtrude","SWEPT_FACE",FACE,{"disambiguationData":[OSD([subQ0])]})],"fromTools":[makeQuery(id+"F31.opExtrude","SWEPT_FACE",FACE,{"disambiguationData":[OSD([subQ0])]})]}),makeQuery(id+"F37.opExtrude","SWEPT_FACE",FACE,{"disambiguationData":[OSD([sQuery(id+"F36.wireOp",EDGE,"E63.right")])]})]})],"fromTools":[makeQuery(id+"F39.opExtrude","SWEPT_FACE",FACE,{"disambiguationData":[OSD([sQuery(id+"F38.wireOp",EDGE,"E65.right")])]})]});}
            var sketch = newSketch(context, id + "F40", { "sketchPlane" : qUnion([Q0])});
            skLineSegment(sketch, "E66", {"start": v(484.15, 900) * mm, "end": v(484.15, 882) * mm});
            skLineSegment(sketch, "E67", {"start": v(484.15, 882) * mm, "end": v(666.15, 700) * mm});
            skLineSegment(sketch, "E68", {"start": v(666.15, 700) * mm, "end": v(684.15, 700) * mm});
            skLineSegment(sketch, "E69", {"start": v(684.15, 700) * mm, "end": v(484.15, 900) * mm});
            skSolve(sketch);
        }
        {
            var Q0;
            Q0 = qSketchRegion(id + "F40", true);
            var Q1;
            {var subQ0=sQuery(id+"F29.wireOp",EDGE,"E50.right");Q1=makeQuery(id+"F39.boolean.opBoolean","MERGE",FACE,{"derivedFrom":[makeQuery(id+"F37.boolean.opBoolean","MERGE",FACE,{"derivedFrom":[makeQuery(id+"F31.boolean.opBoolean","MERGE",FACE,{"derivedFrom":[makeQuery(id+"F28.opExtrude","SWEPT_FACE",FACE,{"disambiguationData":[OSD([sQuery(id+"F27.wireOp",EDGE,"E46")])]}),makeQuery(id+"F30.opExtrude","SWEPT_FACE",FACE,{"disambiguationData":[OSD([subQ0])]})],"fromTools":[makeQuery(id+"F31.opExtrude","SWEPT_FACE",FACE,{"disambiguationData":[OSD([subQ0])]})]}),makeQuery(id+"F37.opExtrude","SWEPT_FACE",FACE,{"disambiguationData":[OSD([sQuery(id+"F36.wireOp",EDGE,"E64.right")])]})]})],"fromTools":[makeQuery(id+"F39.opExtrude","SWEPT_FACE",FACE,{"disambiguationData":[OSD([sQuery(id+"F38.wireOp",EDGE,"E65.left")])]})]});}
            extrude(context, id + "F41", {"entities" : qUnion([Q0]), "endBound" : BoundingType.UP_TO_SURFACE, "depth" : 25 * mm, "endBoundEntityFace" : qUnion([Q1]), "offsetDistance" : 25 * mm});
        }
        {
            var Q0;
            Q0=makeQuery(id+"F30.boolean.opBoolean","MERGE",FACE,{"derivedFrom":[makeQuery(id+"F28.opExtrude","CAP_FACE",FACE,{"disambiguationData":[OSD([sQuery(id+"F27.wireOp",EDGE,"E41"),sQuery(id+"F27.wireOp",EDGE,"E42"),sQuery(id+"F27.wireOp",EDGE,"E43"),sQuery(id+"F27.wireOp",EDGE,"E44"),sQuery(id+"F27.wireOp",EDGE,"E45"),sQuery(id+"F27.wireOp",EDGE,"E46"),sQuery(id+"F27.wireOp",EDGE,"E47"),sQuery(id+"F27.wireOp",EDGE,"E48")])],"isStart":false}),makeQuery(id+"F30.opExtrude","SWEPT_FACE",FACE,{"disambiguationData":[OSD([sQuery(id+"F29.wireOp",EDGE,"E50.top"),sQuery(id+"F29.wireOp",EDGE,"E52.top"),sQuery(id+"F29.wireOp",EDGE,"E54.bottom")])]})]});
            var sketch = newSketch(context, id + "F42", { "sketchPlane" : qUnion([Q0])});
            skPoint(sketch, "E70", {"position": v(-188.7, 0) * mm});
            skPoint(sketch, "E71", {"position": v(175.3, 0) * mm});
            skLineSegment(sketch, "E72", {"start": v(-188.7, 0) * mm, "end": v(-188.7, 182) * mm});
            skLineSegment(sketch, "E73", {"start": v(-188.7, 182) * mm, "end": v(175.3, 182) * mm});
            skLineSegment(sketch, "E74", {"start": v(175.3, 182) * mm, "end": v(175.3, 0) * mm});
            skLineSegment(sketch, "E75", {"start": v(-188.7, 0) * mm, "end": v(175.3, 0) * mm});
            skLineSegment(sketch, "E76", {"start": v(-206.7, -18) * mm, "end": v(-206.7, 200) * mm});
            skLineSegment(sketch, "E77", {"start": v(-206.7, 200) * mm, "end": v(193.3, 200) * mm});
            skLineSegment(sketch, "E78", {"start": v(193.3, 200) * mm, "end": v(193.3, -18) * mm});
            skLineSegment(sketch, "E79", {"start": v(193.3, -18) * mm, "end": v(-206.7, -18) * mm});
            skSolve(sketch);
        }
        {
            var Q0;
            Q0=makeQuery(id+"F42.imprint","IMPRINT",FACE,{"disambiguationData":[TD([[makeQuery(id+"F42.imprint","IMPRINT",EDGE,{"derivedFrom":sQuery(id+"F42.wireOp",EDGE,"E72")}),-1.0]])]});
            extrude(context, id + "F43", {"entities" : qUnion([Q0]), "operationType" : NewBodyOperationType.REMOVE, "oppositeDirection" : true, "depth" : 25 * mm, "offsetDistance" : 25 * mm});
        }
        {
            var Q0;
            Q0=makeQuery(id+"F42.imprint","IMPRINT",FACE,{"disambiguationData":[TD([[makeQuery(id+"F42.imprint","IMPRINT",EDGE,{"derivedFrom":sQuery(id+"F42.wireOp",EDGE,"E72")}),1.0]])]});
            extrude(context, id + "F44", {"entities" : qUnion([Q0]), "operationType" : NewBodyOperationType.ADD, "depth" : 200 * mm, "offsetDistance" : 25 * mm});
        }
        {
            var Q0;
            Q0=makeQuery(id+"F44.boolean.opBoolean","MERGE",FACE,{"derivedFrom":[makeQuery(id+"F37.boolean.opBoolean","MERGE",FACE,{"derivedFrom":[makeQuery(id+"F30.boolean.opBoolean","MERGE",FACE,{"derivedFrom":[makeQuery(id+"F28.opExtrude","SWEPT_FACE",FACE,{"disambiguationData":[OSD([sQuery(id+"F27.wireOp",EDGE,"E43")])]}),makeQuery(id+"F30.opExtrude","SWEPT_FACE",FACE,{"disambiguationData":[OSD([sQuery(id+"F29.wireOp",EDGE,"E50.left")])]})]}),makeQuery(id+"F37.opExtrude","SWEPT_FACE",FACE,{"disambiguationData":[OSD([sQuery(id+"F36.wireOp",EDGE,"E61.right"),sQuery(id+"F36.wireOp",EDGE,"E62.left"),sQuery(id+"F36.wireOp",EDGE,"E64.left")])]})]}),makeQuery(id+"F44.opExtrude","SWEPT_FACE",FACE,{"disambiguationData":[OSD([sQuery(id+"F42.wireOp",EDGE,"E76")])]})]});
            var sketch = newSketch(context, id + "F45", { "sketchPlane" : qUnion([Q0])});
            skPoint(sketch, "E80", {"position": v(684.15, -18) * mm});
            skPoint(sketch, "E81", {"position": v(484.15, 200) * mm});
            skLineSegment(sketch, "E82", {"start": v(484.15, 200) * mm, "end": v(684.15, -18) * mm});
            skSolve(sketch);
        }
        {
            var Q0;
            {var subQ0=sQuery(id+"F45.wireOp",EDGE,"E82");Q0=makeQuery(id+"F45.imprint","IMPRINT",FACE,{"disambiguationData":[TD([[makeQuery(id+"F45.imprint","IMPRINT",EDGE,{"derivedFrom":subQ0}),-1.0]])]});}
            extrude(context, id + "F46", {"entities" : qUnion([Q0]), "operationType" : NewBodyOperationType.REMOVE, "endBound" : BoundingType.THROUGH_ALL, "oppositeDirection" : true, "depth" : 25 * mm, "offsetDistance" : 25 * mm});
        }
        {
            var Q0;
            Q0=makeQuery(id+"F46.boolean.opBoolean","COPY",FACE,{"derivedFrom":makeQuery(id+"F46.opExtrude","SWEPT_FACE",FACE,{"disambiguationData":[OSD([sQuery(id+"F45.wireOp",EDGE,"E82")])]})});
            var sketch = newSketch(context, id + "F47", { "sketchPlane" : qUnion([Q0])});
            skLineSegment(sketch, "E83.bottom", {"start": v(-193.3, -179.92) * mm, "end": v(206.7, -179.92) * mm});
            skLineSegment(sketch, "E83.top", {"start": v(-193.3, -475.77) * mm, "end": v(206.7, -475.77) * mm});
            skLineSegment(sketch, "E83.left", {"start": v(-193.3, -179.92) * mm, "end": v(-193.3, -475.77) * mm});
            skLineSegment(sketch, "E83.right", {"start": v(206.7, -179.92) * mm, "end": v(206.7, -475.77) * mm});
            skSolve(sketch);
        }
        {
            var Q0;
            Q0 = qSketchRegion(id + "F47", true);
            extrude(context, id + "F48", {"entities" : qUnion([Q0]), "depth" : 4 * mm, "offsetDistance" : 25 * mm});
        }
    });
